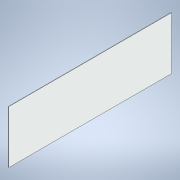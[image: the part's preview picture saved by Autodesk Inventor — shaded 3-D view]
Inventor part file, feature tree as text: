
AUTODESK INVENTOR PART (.ipt)
format: ipt  version: 2022 (Build 260153000, 153)  size: 100,352 bytes
history: native  units: mm
features: extrude x1, sketch x1
ambient origin geometry x8: Origin, YZ Plane, XZ Plane, XY Plane, X Axis, Y Axis, Z Axis, Center Point
bodies: Solid1 (feature_tree)
feature tree (2):
  extrude  "Extrusion1"  Depth=1118.0mm
  sketch  "Sketch1"  dims[d0=470.0mm d1=1118.0mm d2=3.0mm d3=0.0mm]
